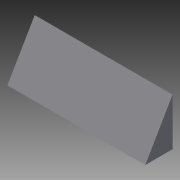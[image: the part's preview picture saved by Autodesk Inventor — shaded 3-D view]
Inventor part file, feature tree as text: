
AUTODESK INVENTOR PART (.ipt)
format: ipt  version: 2014 SP1 (Build 180222100, 222)  size: 66,048 bytes
history: native  units: in
note: dims shown in document units (in); Inventor stores cm internally (conversion verified against a paired STEP export)
features: extrude x1, sketch x1
ambient origin geometry x8: Origin, YZ Plane, XZ Plane, XY Plane, X Axis, Y Axis, Z Axis, Center Point
bodies: Solid1 (feature_tree)
feature tree (2):
  extrude  "Extrusion1"  Depth=5.825in
  sketch  "Sketch1"  dims[d0=3.363in d1=5.825in d2=17.0in d3=0.0in]
